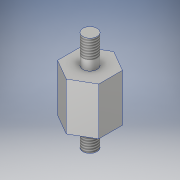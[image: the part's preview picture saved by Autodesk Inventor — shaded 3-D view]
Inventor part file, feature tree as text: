
AUTODESK INVENTOR PART (.ipt)
format: ipt  version: 2018 (Build 220112000, 112)  size: 115,712 bytes
history: native  units: in
note: dims shown in document units (in); Inventor stores cm internally (conversion verified against a paired STEP export)
features: extrude x3, sketch x3, thread x2
ambient origin geometry x8: Origin, YZ Plane, XZ Plane, XY Plane, X Axis, Y Axis, Z Axis, Center Point
bodies: Solid1 (feature_tree)
feature tree (8):
  extrude  "Extrusion1"  Depth=0.3937in TaperAngle=0.0deg
  extrude  "Extrusion2"  Depth=0.2362in TaperAngle=0.0deg
  extrude  "Extrusion3"  Depth=0.1969in TaperAngle=0.0deg
  thread  "Thread1"  [1 undecoded]
  thread  "Thread2"  [1 undecoded]
  sketch  "Sketch1"  dims[d1=0.1969in d2=0.3937in d3=0.0in]
  sketch  "Sketch2"  dims[d4=0.1181in d5=0.2362in d6=0.0in]
  sketch  "Sketch3"  dims[d7=0.1181in d8=0.1969in d9=0.0in d10=0.1575in d11=0.0in d12=0.3937in d13=0.0in]
note: 2 required parameter values undecoded (feature->parameter linkage not recoverable at this tier; creation-order binding heuristic only, values carry confidence <= 0.55)
